# Revit family: IS_Connect_E8105_BIM_DE
name_source: partatom
category: Plumbing Fixtures
revit_build: Autodesk Revit MEP 2014 (Build: 20130308_1515(x64)
units: mm (PartAtom-declared; Revit-internal decimal feet)

## types (4) — shared parameters
Accessories = www.idealstandard.de\ersatzteile
AreaUnits = millimeters
Assembly Code = C1030200
AssetType = Fixed
Brand = Ideal Standard
CodePerformance = DIN EN 14688 CL 00, DIN EN 31
ConnectionType = Plumbing
Default Elevation = 850 mm  [stored 2.78871 ft]
DrainSize = 42 mm  [stored 0.137795 ft]
DurationUnit = year
ExpectedLife = 25
Features = Connect Cube 65cm washbasin, without taphole and overflow
GrossWeight = 0
IfcExportAs = IfcSanitaryType
IfcExportType = WASHHANDBASIN
InstallationInstructions = www.idealstandard.de\produkte
LinearUnits = millimeters
ManufacturerURL = www.idealstandard.de
Material = Vitreous china
NBSDescription = Pedestal wash basins
NBSReference = 45-35-70/365
NettWeight = 20 kg
NominalHeight = 155 mm  [stored 0.50853 ft]
NominalLength = 460 mm  [stored 1.50919 ft]
NominalWidth = 650 mm  [stored 2.13255 ft]
ProductInformation = www.idealstandard.de\produkte
Shape = Sculptured
Size = 650x460x155mm
Space = Internal
URL = www.idealstandard.com
Uniclass2015Code = Pr_40_20_96_63
Uniclass2015Title = Pedestal wash basins
Uniclass2015Version = Products v1.1
Version = 1
VolumeUnits = Litres
WarrantyDescription = Manufacturers Warranty
WarrantyDurationUnit = year
WashHandBasinMounting = i.e.Wall Hung
WashHandBasinType = Hand Rinse
zero-valued in all types: CWFU, Cost, HWFU, WFU

## per-type parameters (varying)
| type | BIMObjectName | BarCode | Color | Description | E7112 | E7113 | Finish | Model | ModelNumber | ModelReference | Name |
| E810501 - Connect Cube 65cm washbasin, without taphole and overflow(E7112) | ISI_IdealStandard_PedestalWashBasins_ConnectCube_E810501 | 5017830406167 | white | E810501 Connect Cube 65cm washbasin, without taphole and overflow | Yes | No | white | E810501 | E810501 | E810501 Connect Cube 65cm washbasin, without taphole and overflow | PedestalWashBasins_ConnectCube_E810501_IdealStandard |
| E810501 - Connect Cube 65cm washbasin, without taphole and overflow(E7113) | ISI_IdealStandard_PedestalWashBasins_ConnectCube_E810501 | 5017830406167 | white | E810501 Connect Cube 65cm washbasin, without taphole and overflow | No | Yes | white | E810501 | E810501 | E810501 Connect Cube 65cm washbasin, without taphole and overflow | PedestalWashBasins_ConnectCube_E810501_IdealStandard |
| E8105MA - Connect Cube 65cm washbasin, without taphole and overflow(E7112) | ISI_IdealStandard_PedestalWashBasins_ConnectCube_E8105MA | 5017830406174 | white with ideal plus | E8105MA Connect Cube 65cm washbasin, without taphole and overflow | Yes | No | white with ideal plus | E8105MA | E8105MA | E8105MA Connect Cube 65cm washbasin, without taphole and overflow | PedestalWashBasins_ConnectCube_E8105MA_IdealStandard |
| E8105MA - Connect Cube 65cm washbasin, without taphole and overflow(E7113) | ISI_IdealStandard_PedestalWashBasins_ConnectCube_E8105MA | 5017830406174 | white with ideal plus | E8105MA Connect Cube 65cm washbasin, without taphole and overflow | No | Yes | white with ideal plus | E8105MA | E8105MA | E8105MA Connect Cube 65cm washbasin, without taphole and overflow | PedestalWashBasins_ConnectCube_E8105MA_IdealStandard |

note: [stored X ft] marks values corroborated as IEEE doubles in the binary element streams (Revit-internal decimal feet)

## geometry (parser evidence)
native form markers: Sweep x9
no freeform markers — native parametric forms only
